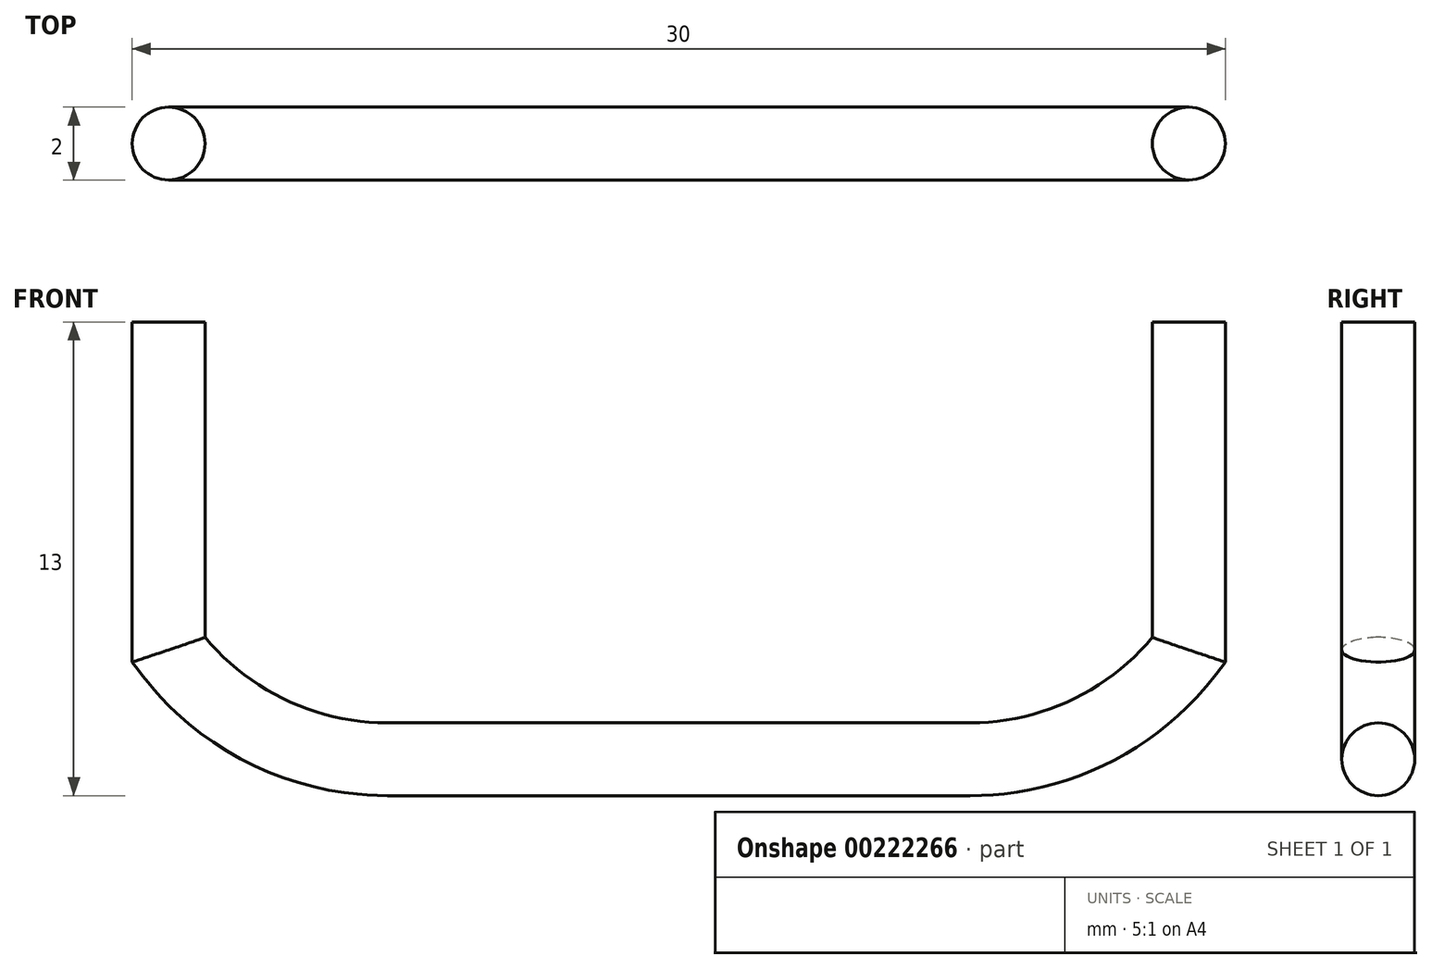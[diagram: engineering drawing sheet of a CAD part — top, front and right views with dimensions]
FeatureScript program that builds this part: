
annotation { "Feature Type Name" : "Feature", "Feature Type Description" : "" }
export const myFeature = defineFeature(function(context is Context, id is Id, definition is map)
    precondition{}
    {
        {
            var Q0;
            Q0=qCreatedBy(makeId("Front.planeOp"),FACE);
            var sketch = newSketch(context, id + "F0", { "sketchPlane" : qUnion([Q0])});
            skLineSegment(sketch, "E0", {"start": v(0, 0) * mm, "end": v(-14, 0) * mm, "construction": true});
            skLineSegment(sketch, "E1", {"start": v(-14, 0) * mm, "end": v(-14, -12) * mm, "construction": true});
            skLineSegment(sketch, "E2", {"start": v(-14, -12) * mm, "end": v(14, -12) * mm, "construction": true});
            skLineSegment(sketch, "E3", {"start": v(14, -12) * mm, "end": v(14, 0) * mm, "construction": true});
            skLineSegment(sketch, "E4", {"start": v(14, -12) * mm, "end": v(14, -9) * mm, "construction": true});
            skLineSegment(sketch, "E5", {"start": v(-14, -12) * mm, "end": v(-8, -12) * mm, "construction": true});
            skLineSegment(sketch, "E6", {"start": v(14, -12) * mm, "end": v(8, -12) * mm, "construction": true});
            skLineSegment(sketch, "E7", {"start": v(-14, -12) * mm, "end": v(-14, -9) * mm, "construction": true});
            skLineSegment(sketch, "E8", {"start": v(-14, 0) * mm, "end": v(-14, -9) * mm});
            skLineSegment(sketch, "E9", {"start": v(-8, -12) * mm, "end": v(8, -12) * mm});
            skLineSegment(sketch, "E10", {"start": v(14, -9) * mm, "end": v(14, 0) * mm});
            skArc(sketch, "E11", {"start": v(-14, -9) * mm, "mid": v(-11.35, -11.2) * mm, "end": v(-8, -12) * mm});
            skArc(sketch, "E12", {"start": v(8, -12) * mm, "mid": v(11.35, -11.2) * mm, "end": v(14, -9) * mm});
            skSolve(sketch);
        }
        {
            var Q0;
            Q0=qCreatedBy(makeId("Top.planeOp"),FACE);
            var sketch = newSketch(context, id + "F1", { "sketchPlane" : qUnion([Q0])});
            skLineSegment(sketch, "E13", {"start": v(0, 0) * mm, "end": v(-14, 0) * mm, "construction": true});
            skCircle(sketch, "E14", {"center": v(-14, 0) * mm, "radius": 1 * mm});
            skSolve(sketch);
        }
        {
            var Q0;
            Q0=makeQuery(id+"F1.imprint","IMPRINT",FACE,{"disambiguationData":[TD([[makeQuery(id+"F1.imprint","IMPRINT",EDGE,{"derivedFrom":sQuery(id+"F1.wireOp",EDGE,"E14")}),1.0]])]});
            var Q1;
            Q1=sQuery(id+"F0.wireOp",EDGE,"E8");
            var Q2;
            Q2=sQuery(id+"F0.wireOp",EDGE,"E11");
            var Q3;
            Q3=sQuery(id+"F0.wireOp",EDGE,"E9");
            var Q4;
            Q4=sQuery(id+"F0.wireOp",EDGE,"E12");
            var Q5;
            Q5=sQuery(id+"F0.wireOp",EDGE,"E10");
            sweep(context, id + "F2", {"profiles" : qUnion([Q0]), "path" : qUnion([Q1, Q2, Q3, Q4, Q5])});
        }
    });
